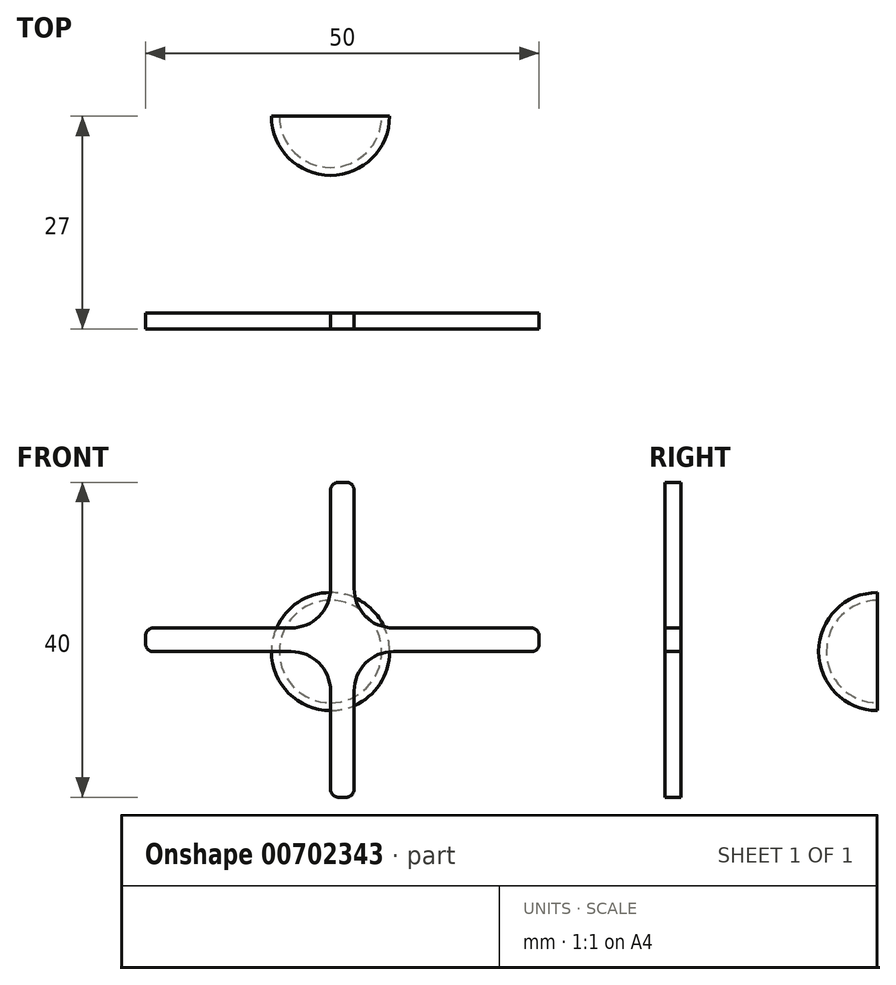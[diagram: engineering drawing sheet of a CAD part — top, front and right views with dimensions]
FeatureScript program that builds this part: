
annotation { "Feature Type Name" : "Feature", "Feature Type Description" : "" }
export const myFeature = defineFeature(function(context is Context, id is Id, definition is map)
    precondition{}
    {
        {
            var Q0;
            Q0=qCreatedBy(makeId("Front.planeOp"),FACE);
            var sketch = newSketch(context, id + "F0", { "sketchPlane" : qUnion([Q0])});
            skCircle(sketch, "E0", {"center": v(0, 0) * mm, "radius": 7.5 * mm});
            skLineSegment(sketch, "E1", {"start": v(0, 12.91) * mm, "end": v(0, -15.24) * mm});
            skCircle(sketch, "E2", {"center": v(0, 0) * mm, "radius": 6.5 * mm});
            skSolve(sketch);
        }
        {
            var Q0;
            {var subQ0=sQuery(id+"F0.wireOp",EDGE,"E1");var subQ1=sQuery(id+"F0.wireOp",EDGE,"E0");var subQ2=makeQuery(id+"F0.imprint","INTERSECT",VERTEX,{"disambiguationData":[OD(0.0)],"derivedFrom":[subQ1,subQ0]});Q0=makeQuery(id+"F0.imprint","IMPRINT",FACE,{"disambiguationData":[TD([[makeQuery(id+"F0.imprint","IMPRINT",EDGE,{"disambiguationData":[TD([[subQ2,-1.0]])],"derivedFrom":subQ1}),1.0]])]});}
            var Q1;
            Q1=sQuery(id+"F0.wireOp",EDGE,"E0");
            var Q2;
            Q2=sQuery(id+"F0.wireOp",EDGE,"E1");
            revolve(context, id + "F1", {"entities" : qUnion([Q0]), "surfaceEntities" : qUnion([Q1]), "axis" : qUnion([Q2]), "revolveType" : RevolveType.ONE_DIRECTION, "angle" : 180 * degree});
        }
        {
            var Q0;
            Q0=qCreatedBy(makeId("Front.planeOp"),FACE);
            cPlane(context, id + "F2", {"entities" : qUnion([Q0]), "cplaneType" : CPlaneType.OFFSET, "offset" : 25 * mm, "width" : 150 * mm, "height" : 150 * mm});
        }
        {
            var Q0;
            Q0=qCreatedBy(makeId("Front.planeOp"),FACE);
            cPlane(context, id + "F3", {"entities" : qUnion([Q0]), "cplaneType" : CPlaneType.OFFSET, "offset" : 50 * mm, "oppositeDirection" : true, "width" : 150 * mm, "height" : 150 * mm});
        }
        {
            var Q0;
            Q0=qCreatedBy(id+"F2.planeOp",FACE);
            var sketch = newSketch(context, id + "F4", { "sketchPlane" : qUnion([Q0])});
            skLineSegment(sketch, "E3.bottom", {"start": v(0, 21.5) * mm, "end": v(3, 21.5) * mm});
            skLineSegment(sketch, "E3.top", {"start": v(0, -18.5) * mm, "end": v(3, -18.5) * mm});
            skLineSegment(sketch, "E3.left", {"start": v(0, 21.5) * mm, "end": v(0, -18.5) * mm});
            skLineSegment(sketch, "E3.right", {"start": v(3, 21.5) * mm, "end": v(3, -18.5) * mm});
            skPoint(sketch, "E3.middle", {"position": v(1.5, 1.5) * mm});
            skLineSegment(sketch, "E4.bottom", {"start": v(-23.5, 0) * mm, "end": v(26.5, 0) * mm});
            skLineSegment(sketch, "E4.top", {"start": v(-23.5, 3) * mm, "end": v(26.5, 3) * mm});
            skLineSegment(sketch, "E4.left", {"start": v(-23.5, 0) * mm, "end": v(-23.5, 3) * mm});
            skLineSegment(sketch, "E4.right", {"start": v(26.5, 0) * mm, "end": v(26.5, 3) * mm});
            skSolve(sketch);
        }
        {
            var Q0;
            {var subQ5=sQuery(id+"F4.wireOp",EDGE,"E4.left");Q0=makeQuery(id+"F4.imprint","IMPRINT",FACE,{"disambiguationData":[TD([[makeQuery(id+"F4.imprint","IMPRINT",EDGE,{"derivedFrom":subQ5}),-1.0]])]});}
            var Q1;
            {var subQ5=sQuery(id+"F4.wireOp",EDGE,"E4.right");Q1=makeQuery(id+"F4.imprint","IMPRINT",FACE,{"disambiguationData":[TD([[makeQuery(id+"F4.imprint","IMPRINT",EDGE,{"derivedFrom":subQ5}),1.0]])]});}
            var Q2;
            {var subQ0=sQuery(id+"F4.wireOp",EDGE,"E3.top");Q2=makeQuery(id+"F4.imprint","IMPRINT",FACE,{"disambiguationData":[TD([[makeQuery(id+"F4.imprint","IMPRINT",EDGE,{"derivedFrom":subQ0}),1.0]])]});}
            var Q3;
            {var subQ0=sQuery(id+"F4.wireOp",EDGE,"E3.bottom");Q3=makeQuery(id+"F4.imprint","IMPRINT",FACE,{"disambiguationData":[TD([[makeQuery(id+"F4.imprint","IMPRINT",EDGE,{"derivedFrom":subQ0}),-1.0]])]});}
            var Q4;
            {var subQ0=sQuery(id+"F4.wireOp",EDGE,"E4.top");var subQ1=sQuery(id+"F4.wireOp",EDGE,"E3.left");var subQ2=makeQuery(id+"F4.imprint","INTERSECT",VERTEX,{"derivedFrom":[subQ1,subQ0]});Q4=makeQuery(id+"F4.imprint","IMPRINT",FACE,{"disambiguationData":[TD([[makeQuery(id+"F4.imprint","IMPRINT",EDGE,{"disambiguationData":[TD([[subQ2,-1.0]])],"derivedFrom":subQ1}),1.0]])]});}
            extrude(context, id + "F5", {"entities" : qUnion([Q0, Q1, Q2, Q3, Q4]), "depth" : 2 * mm, "offsetDistance" : 25 * mm});
        }
        {
            var Q0;
            Q0=makeQuery(id+"F5.opExtrude","SWEPT_EDGE",EDGE,{"disambiguationData":[OSD([sQuery(id+"F4.wireOp",EDGE,"E3.left"),sQuery(id+"F4.wireOp",EDGE,"E4.top")])]});
            var Q1;
            Q1=makeQuery(id+"F5.opExtrude","SWEPT_EDGE",EDGE,{"disambiguationData":[OSD([sQuery(id+"F4.wireOp",EDGE,"E3.left"),sQuery(id+"F4.wireOp",EDGE,"E4.bottom")])]});
            var Q2;
            Q2=makeQuery(id+"F5.opExtrude","SWEPT_EDGE",EDGE,{"disambiguationData":[OSD([sQuery(id+"F4.wireOp",EDGE,"E3.right"),sQuery(id+"F4.wireOp",EDGE,"E4.bottom")])]});
            var Q3;
            Q3=makeQuery(id+"F5.opExtrude","SWEPT_EDGE",EDGE,{"disambiguationData":[OSD([sQuery(id+"F4.wireOp",EDGE,"E3.right"),sQuery(id+"F4.wireOp",EDGE,"E4.top")])]});
            fillet(context, id + "F6", {"entities" : qUnion([Q0, Q1, Q2, Q3]), "radius" : 5 * mm, "tangentPropagation" : true, "allowEdgeOverflow" : false});
        }
        {
            var Q0;
            Q0=makeQuery(id+"F5.opExtrude","SWEPT_EDGE",EDGE,{"disambiguationData":[OSD([sQuery(id+"F4.wireOp",EDGE,"E3.bottom"),sQuery(id+"F4.wireOp",EDGE,"E3.right")])]});
            var Q1;
            Q1=makeQuery(id+"F5.opExtrude","SWEPT_EDGE",EDGE,{"disambiguationData":[OSD([sQuery(id+"F4.wireOp",EDGE,"E3.bottom"),sQuery(id+"F4.wireOp",EDGE,"E3.left")])]});
            var Q2;
            Q2=makeQuery(id+"F5.opExtrude","SWEPT_EDGE",EDGE,{"disambiguationData":[OSD([sQuery(id+"F4.wireOp",EDGE,"E4.top"),sQuery(id+"F4.wireOp",EDGE,"E4.right")])]});
            var Q3;
            Q3=makeQuery(id+"F5.opExtrude","SWEPT_EDGE",EDGE,{"disambiguationData":[OSD([sQuery(id+"F4.wireOp",EDGE,"E4.bottom"),sQuery(id+"F4.wireOp",EDGE,"E4.right")])]});
            var Q4;
            Q4=makeQuery(id+"F5.opExtrude","SWEPT_EDGE",EDGE,{"disambiguationData":[OSD([sQuery(id+"F4.wireOp",EDGE,"E3.top"),sQuery(id+"F4.wireOp",EDGE,"E3.right")])]});
            var Q5;
            Q5=makeQuery(id+"F5.opExtrude","SWEPT_EDGE",EDGE,{"disambiguationData":[OSD([sQuery(id+"F4.wireOp",EDGE,"E3.top"),sQuery(id+"F4.wireOp",EDGE,"E3.left")])]});
            var Q6;
            Q6=makeQuery(id+"F5.opExtrude","SWEPT_EDGE",EDGE,{"disambiguationData":[OSD([sQuery(id+"F4.wireOp",EDGE,"E4.top"),sQuery(id+"F4.wireOp",EDGE,"E4.left")])]});
            var Q7;
            Q7=makeQuery(id+"F5.opExtrude","SWEPT_EDGE",EDGE,{"disambiguationData":[OSD([sQuery(id+"F4.wireOp",EDGE,"E4.bottom"),sQuery(id+"F4.wireOp",EDGE,"E4.left")])]});
            fillet(context, id + "F7", {"entities" : qUnion([Q0, Q1, Q2, Q3, Q4, Q5, Q6, Q7]), "radius" : 1 * mm, "tangentPropagation" : true, "allowEdgeOverflow" : false});
        }
    });
